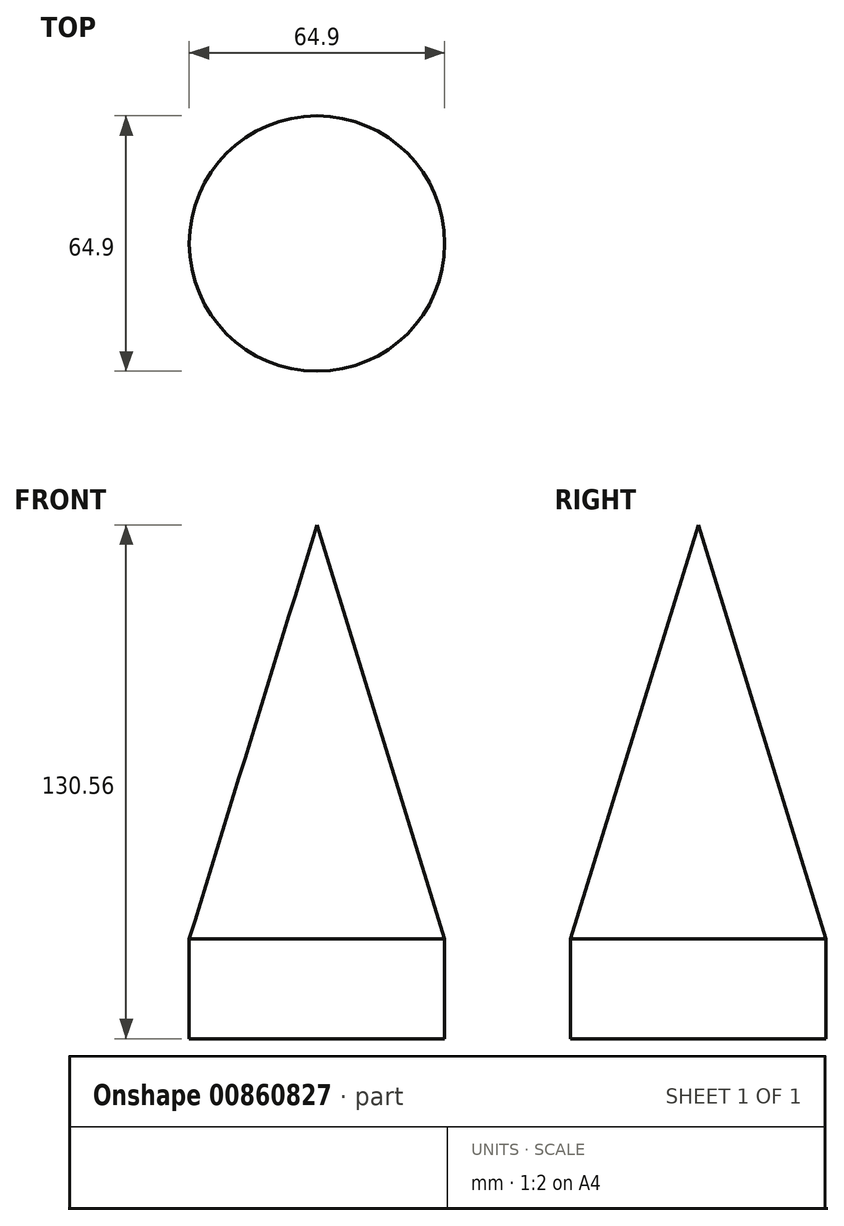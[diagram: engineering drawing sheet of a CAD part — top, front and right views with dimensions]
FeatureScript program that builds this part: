
annotation { "Feature Type Name" : "Feature", "Feature Type Description" : "" }
export const myFeature = defineFeature(function(context is Context, id is Id, definition is map)
    precondition{}
    {
        {
            var Q0;
            Q0=qCreatedBy(makeId("Front.planeOp"),FACE);
            var sketch = newSketch(context, id + "F0", { "sketchPlane" : qUnion([Q0])});
            skLineSegment(sketch, "E0", {"start": v(-3.5, 53.44) * mm, "end": v(-3.5, -51.72) * mm});
            skLineSegment(sketch, "E1", {"start": v(-3.5, -51.72) * mm, "end": v(28.96, -51.72) * mm});
            skLineSegment(sketch, "E2", {"start": v(28.96, -51.72) * mm, "end": v(-3.5, 53.44) * mm});
            skSolve(sketch);
        }
        {
            var Q0;
            Q0=makeQuery(id+"F0.imprint","IMPRINT",FACE,{"disambiguationData":[TD([[makeQuery(id+"F0.imprint","IMPRINT",EDGE,{"derivedFrom":sQuery(id+"F0.wireOp",EDGE,"E0")}),1.0]])]});
            var Q1;
            Q1=sQuery(id+"F0.wireOp",EDGE,"E0");
            revolve(context, id + "F1", {"surfaceOperationType" : NewSurfaceOperationType.NEW, "entities" : qUnion([Q0]), "axis" : qUnion([Q1]), "revolveType" : RevolveType.FULL});
        }
        {
            var Q0;
            Q0=makeQuery(id+"F1.opRevolve","SWEPT_FACE",FACE,{"disambiguationData":[OSD([sQuery(id+"F0.wireOp",EDGE,"E1")])]});
            extrude(context, id + "F2", {"entities" : qUnion([Q0]), "operationType" : NewBodyOperationType.ADD, "depth" : 25.4 * mm, "offsetDistance" : 25.4 * mm});
        }
    });
